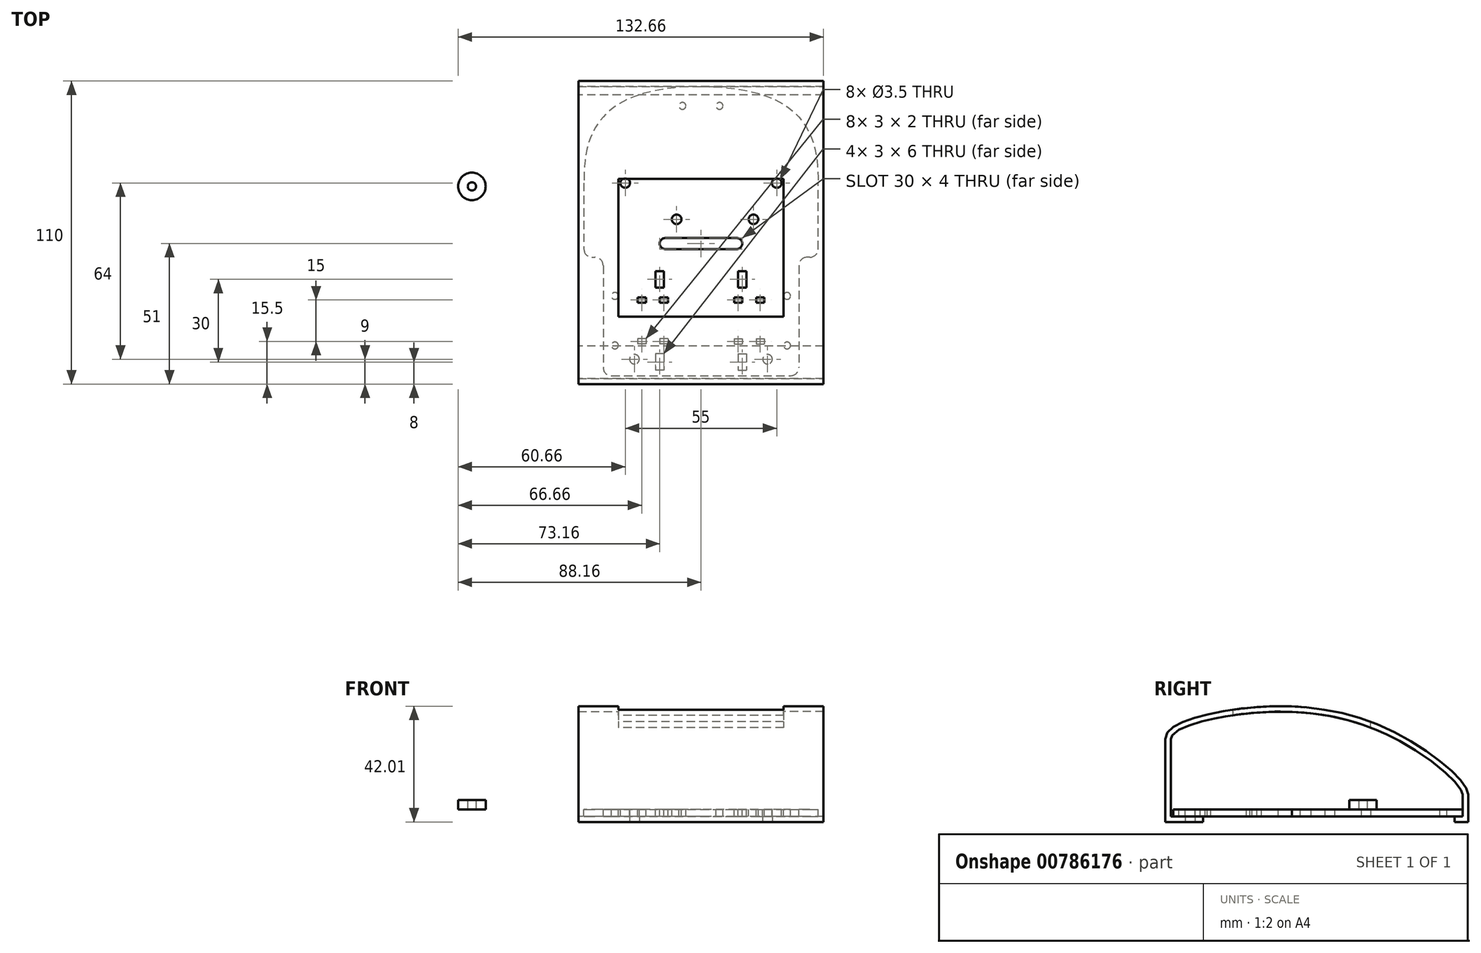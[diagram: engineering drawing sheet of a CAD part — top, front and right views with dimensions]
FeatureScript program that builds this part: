
annotation { "Feature Type Name" : "Feature", "Feature Type Description" : "" }
export const myFeature = defineFeature(function(context is Context, id is Id, definition is map)
    precondition{}
    {
        {
            var Q0;
            Q0=qCreatedBy(makeId("Top.planeOp"),FACE);
            var sketch = newSketch(context, id + "F0", { "sketchPlane" : qUnion([Q0])});
            skPoint(sketch, "E0.middle", {"position": v(0, 0) * mm});
            skLineSegment(sketch, "E1", {"start": v(4.5, 6) * mm, "end": v(31.5, 6) * mm});
            skLineSegment(sketch, "E2", {"start": v(31.5, 6) * mm, "end": v(31.5, -6) * mm});
            skLineSegment(sketch, "E3", {"start": v(31.5, -6) * mm, "end": v(5.5, -6) * mm});
            skLineSegment(sketch, "E4.bottom", {"start": v(20, 6.5) * mm, "end": v(17, 6.5) * mm});
            skLineSegment(sketch, "E4.top", {"start": v(20, 8.5) * mm, "end": v(17, 8.5) * mm});
            skLineSegment(sketch, "E4.left", {"start": v(20, 6.5) * mm, "end": v(20, 8.5) * mm});
            skLineSegment(sketch, "E4.right", {"start": v(17, 6.5) * mm, "end": v(17, 8.5) * mm});
            skPoint(sketch, "E4.middle", {"position": v(18.5, 7.5) * mm});
            skLineSegment(sketch, "E5.bottom", {"start": v(25, 8.5) * mm, "end": v(28, 8.5) * mm});
            skLineSegment(sketch, "E5.top", {"start": v(25, 6.5) * mm, "end": v(28, 6.5) * mm});
            skLineSegment(sketch, "E5.left", {"start": v(25, 8.5) * mm, "end": v(25, 6.5) * mm});
            skLineSegment(sketch, "E5.right", {"start": v(28, 8.5) * mm, "end": v(28, 6.5) * mm});
            skPoint(sketch, "E5.middle", {"position": v(26.5, 7.5) * mm});
            skLineSegment(sketch, "E6", {"start": v(40, -20) * mm, "end": v(40, -20) * mm});
            skLineSegment(sketch, "E7.bottom", {"start": v(26.5, -12) * mm, "end": v(23.5, -12) * mm});
            skLineSegment(sketch, "E7.top", {"start": v(26.5, -18) * mm, "end": v(23.5, -18) * mm});
            skLineSegment(sketch, "E7.left", {"start": v(26.5, -12) * mm, "end": v(26.5, -18) * mm});
            skLineSegment(sketch, "E7.right", {"start": v(23.5, -12) * mm, "end": v(23.5, -18) * mm});
            skPoint(sketch, "E7.middle", {"position": v(25, -15) * mm});
            skLineSegment(sketch, "E8.bottom", {"start": v(23.5, 12) * mm, "end": v(26.5, 12) * mm});
            skLineSegment(sketch, "E8.top", {"start": v(23.5, 18) * mm, "end": v(26.5, 18) * mm});
            skLineSegment(sketch, "E8.left", {"start": v(23.5, 12) * mm, "end": v(23.5, 18) * mm});
            skLineSegment(sketch, "E8.right", {"start": v(26.5, 12) * mm, "end": v(26.5, 18) * mm});
            skPoint(sketch, "E8.middle", {"position": v(25, 15) * mm});
            skCircle(sketch, "E9", {"center": v(8.75, 9) * mm, "radius": 1.25 * mm});
            skCircle(sketch, "E10", {"center": v(8.75, -9) * mm, "radius": 1.25 * mm});
            skCircle(sketch, "E11", {"center": v(12.5, 50) * mm, "radius": 1.75 * mm});
            skLineSegment(sketch, "E12", {"start": v(0.5, 23) * mm, "end": v(1.5, 23) * mm});
            skLineSegment(sketch, "E13", {"start": v(4.5, 20) * mm, "end": v(4.5, -17) * mm});
            skLineSegment(sketch, "E14", {"start": v(7.5, -20) * mm, "end": v(40, -20) * mm});
            skLineSegment(sketch, "E15", {"start": v(40, 85) * mm, "end": v(-2.5, 85) * mm});
            skLineSegment(sketch, "E16", {"start": v(-2.5, 85) * mm, "end": v(-2.5, 26) * mm});
            skLineSegment(sketch, "E17", {"start": v(40, -20) * mm, "end": v(40, 85) * mm, "construction": true});
            skLineSegment(sketch, "E18", {"start": v(7.5, 60) * mm, "end": v(7.5, 65) * mm});
            skLineSegment(sketch, "E19", {"start": v(12.5, 70) * mm, "end": v(40, 70) * mm});
            skLineSegment(sketch, "E20", {"start": v(19.5, 48) * mm, "end": v(40, 48) * mm});
            skLineSegment(sketch, "E21", {"start": v(17.5, 50) * mm, "end": v(17.5, 50) * mm});
            skLineSegment(sketch, "E22", {"start": v(12.5, 55) * mm, "end": v(12.5, 55) * mm});
            skCircle(sketch, "E23", {"center": v(33.27, 78) * mm, "radius": 1.25 * mm});
            skPoint(sketch, "E24.visualSharp", {"position": v(7.5, 70) * mm});
            skArc(sketch, "E24.filletArc", {"start": v(12.5, 70) * mm, "mid": v(8.96, 68.54) * mm, "end": v(7.5, 65) * mm});
            skPoint(sketch, "E25.visualSharp", {"position": v(7.5, 55) * mm});
            skArc(sketch, "E25.filletArc", {"start": v(7.5, 60) * mm, "mid": v(8.96, 56.46) * mm, "end": v(12.5, 55) * mm});
            skPoint(sketch, "E26.visualSharp", {"position": v(17.5, 55) * mm});
            skArc(sketch, "E26.filletArc", {"start": v(17.5, 50) * mm, "mid": v(16.04, 53.54) * mm, "end": v(12.5, 55) * mm});
            skPoint(sketch, "E27.visualSharp", {"position": v(17.5, 48) * mm});
            skArc(sketch, "E27.filletArc", {"start": v(17.5, 50) * mm, "mid": v(18.09, 48.59) * mm, "end": v(19.5, 48) * mm});
            skPoint(sketch, "E28.visualSharp", {"position": v(-2.5, 23) * mm});
            skArc(sketch, "E28.filletArc", {"start": v(-2.5, 26) * mm, "mid": v(-1.62, 23.88) * mm, "end": v(0.5, 23) * mm});
            skPoint(sketch, "E29.visualSharp", {"position": v(4.5, 23) * mm});
            skArc(sketch, "E29.filletArc", {"start": v(4.5, 20) * mm, "mid": v(3.62, 22.12) * mm, "end": v(1.5, 23) * mm});
            skPoint(sketch, "E30.visualSharp", {"position": v(4.5, -20) * mm});
            skArc(sketch, "E30.filletArc", {"start": v(4.5, -17) * mm, "mid": v(5.38, -19.12) * mm, "end": v(7.5, -20) * mm});
            skCircle(sketch, "E31", {"center": v(15.85, -14) * mm, "radius": 1.75 * mm});
            skCircle(sketch, "E32", {"center": v(64.15, -14) * mm, "radius": 1.75 * mm});
            skCircle(sketch, "E33", {"center": v(59.05, 36.8) * mm, "radius": 1.75 * mm});
            skCircle(sketch, "E34", {"center": v(31.15, 36.8) * mm, "radius": 1.75 * mm});
            skLineSegment(sketch, "E35.bottom", {"start": v(-2.5, -20) * mm, "end": v(2.5, -20) * mm});
            skLineSegment(sketch, "E35.top", {"start": v(-2.5, 20) * mm, "end": v(2.5, 20) * mm});
            skLineSegment(sketch, "E35.left", {"start": v(-2.5, -20) * mm, "end": v(-2.5, 20) * mm});
            skLineSegment(sketch, "E35.right", {"start": v(2.5, -20) * mm, "end": v(2.5, 20) * mm});
            skLineSegment(sketch, "E36", {"start": v(0, 0) * mm, "end": v(100, 0) * mm, "construction": true});
            skLineSegment(sketch, "E37.bottom", {"start": v(28, -6.5) * mm, "end": v(25, -6.5) * mm});
            skLineSegment(sketch, "E37.top", {"start": v(28, -8.5) * mm, "end": v(25, -8.5) * mm});
            skLineSegment(sketch, "E37.left", {"start": v(28, -6.5) * mm, "end": v(28, -8.5) * mm});
            skLineSegment(sketch, "E37.right", {"start": v(25, -6.5) * mm, "end": v(25, -8.5) * mm});
            skPoint(sketch, "E37.middle", {"position": v(26.5, -7.5) * mm});
            skLineSegment(sketch, "E38.bottom", {"start": v(20, -6.5) * mm, "end": v(17, -6.5) * mm});
            skLineSegment(sketch, "E38.top", {"start": v(20, -8.5) * mm, "end": v(17, -8.5) * mm});
            skLineSegment(sketch, "E38.left", {"start": v(20, -6.5) * mm, "end": v(20, -8.5) * mm});
            skLineSegment(sketch, "E38.right", {"start": v(17, -6.5) * mm, "end": v(17, -8.5) * mm});
            skPoint(sketch, "E38.middle", {"position": v(18.5, -7.5) * mm});
            skPoint(sketch, "E38.middle.positionSnap0", {"position": v(18.5, 6.5) * mm});
            skPoint(sketch, "E38.centerSnap0", {"position": v(18.5, 6.5) * mm});
            skFitSpline(sketch, "E39", {"points": [v(40, 85) * mm, v(-2.5, 50) * mm], "startDerivative": vector(-120, 0) * mm, "endDerivative": vector(0, -45) * mm});
            skLineSegment(sketch, "E40", {"start": v(40, 30) * mm, "end": v(27, 30) * mm});
            skLineSegment(sketch, "E41", {"start": v(25, 28) * mm, "end": v(25, 28) * mm});
            skLineSegment(sketch, "E42", {"start": v(27, 26) * mm, "end": v(40, 26) * mm});
            skPoint(sketch, "E43.visualSharp", {"position": v(25, 26) * mm});
            skArc(sketch, "E43.filletArc", {"start": v(25, 28) * mm, "mid": v(25.59, 26.59) * mm, "end": v(27, 26) * mm});
            skPoint(sketch, "E44.visualSharp", {"position": v(25, 30) * mm});
            skArc(sketch, "E44.filletArc", {"start": v(27, 30) * mm, "mid": v(25.59, 29.41) * mm, "end": v(25, 28) * mm});
            skArc(sketch, "E45.MirrorCS", {"start": v(82.5, 26) * mm, "mid": v(81.62, 23.88) * mm, "end": v(79.5, 23) * mm});
            skArc(sketch, "E46.MirrorCS", {"start": v(75.5, 20) * mm, "mid": v(76.38, 22.12) * mm, "end": v(78.5, 23) * mm});
            skLineSegment(sketch, "E47.MirrorCS", {"start": v(82.5, 20) * mm, "end": v(77.5, 20) * mm});
            skArc(sketch, "E48.MirrorCS", {"start": v(53, 30) * mm, "mid": v(54.41, 29.41) * mm, "end": v(55, 28) * mm});
            skLineSegment(sketch, "E49.MirrorCS", {"start": v(60, 6.5) * mm, "end": v(63, 6.5) * mm});
            skLineSegment(sketch, "E50.MirrorCS", {"start": v(55, -6.5) * mm, "end": v(55, -8.5) * mm});
            skLineSegment(sketch, "E51.MirrorCS", {"start": v(60, 8.5) * mm, "end": v(63, 8.5) * mm});
            skLineSegment(sketch, "E52.MirrorCS", {"start": v(60, 6.5) * mm, "end": v(60, 8.5) * mm});
            skArc(sketch, "E53.MirrorCS", {"start": v(55, 28) * mm, "mid": v(54.41, 26.59) * mm, "end": v(53, 26) * mm});
            skLineSegment(sketch, "E54.MirrorCS", {"start": v(55, 8.5) * mm, "end": v(55, 6.5) * mm});
            skLineSegment(sketch, "E55.MirrorCS", {"start": v(60, -6.5) * mm, "end": v(60, -8.5) * mm});
            skLineSegment(sketch, "E56.MirrorCS", {"start": v(63, 6.5) * mm, "end": v(63, 8.5) * mm});
            skLineSegment(sketch, "E57.MirrorCS", {"start": v(52, 8.5) * mm, "end": v(52, 6.5) * mm});
            skLineSegment(sketch, "E58.MirrorCS", {"start": v(52, -8.5) * mm, "end": v(55, -8.5) * mm});
            skLineSegment(sketch, "E59.MirrorCS", {"start": v(56.5, 18) * mm, "end": v(53.5, 18) * mm});
            skLineSegment(sketch, "E60.MirrorCS", {"start": v(53.5, -12) * mm, "end": v(56.5, -12) * mm});
            skLineSegment(sketch, "E61.MirrorCS", {"start": v(60, -8.5) * mm, "end": v(63, -8.5) * mm});
            skLineSegment(sketch, "E62.MirrorCS", {"start": v(63, -6.5) * mm, "end": v(63, -8.5) * mm});
            skLineSegment(sketch, "E63.MirrorCS", {"start": v(56.5, 12) * mm, "end": v(53.5, 12) * mm});
            skLineSegment(sketch, "E64.MirrorCS", {"start": v(60, -6.5) * mm, "end": v(63, -6.5) * mm});
            skLineSegment(sketch, "E65.MirrorCS", {"start": v(53.5, 12) * mm, "end": v(53.5, 18) * mm});
            skArc(sketch, "E66.MirrorCS", {"start": v(75.5, -17) * mm, "mid": v(74.62, -19.12) * mm, "end": v(72.5, -20) * mm});
            skLineSegment(sketch, "E67.MirrorCS", {"start": v(55, 8.5) * mm, "end": v(52, 8.5) * mm});
            skLineSegment(sketch, "E68.MirrorCS", {"start": v(55, 6.5) * mm, "end": v(52, 6.5) * mm});
            skLineSegment(sketch, "E69.MirrorCS", {"start": v(52, -6.5) * mm, "end": v(55, -6.5) * mm});
            skLineSegment(sketch, "E70.MirrorCS", {"start": v(56.5, 12) * mm, "end": v(56.5, 18) * mm});
            skArc(sketch, "E71.MirrorCS", {"start": v(62.5, 50) * mm, "mid": v(63.96, 53.54) * mm, "end": v(67.5, 55) * mm});
            skLineSegment(sketch, "E72.MirrorCS", {"start": v(52, -6.5) * mm, "end": v(52, -8.5) * mm});
            skLineSegment(sketch, "E73.MirrorCS", {"start": v(67.5, 55) * mm, "end": v(67.5, 55) * mm});
            skCircle(sketch, "E74.MirrorC", {"center": v(67.5, 50) * mm, "radius": 1.75 * mm});
            skLineSegment(sketch, "E75.MirrorCS", {"start": v(53.5, -18) * mm, "end": v(56.5, -18) * mm});
            skLineSegment(sketch, "E76.MirrorCS", {"start": v(56.5, -12) * mm, "end": v(56.5, -18) * mm});
            skLineSegment(sketch, "E77.MirrorCS", {"start": v(75.5, 6) * mm, "end": v(48.5, 6) * mm});
            skCircle(sketch, "E78.MirrorC", {"center": v(71.25, 9) * mm, "radius": 1.25 * mm});
            skArc(sketch, "E79.MirrorCS", {"start": v(67.5, 70) * mm, "mid": v(71.04, 68.54) * mm, "end": v(72.5, 65) * mm});
            skLineSegment(sketch, "E80.MirrorCS", {"start": v(53.5, -12) * mm, "end": v(53.5, -18) * mm});
            skLineSegment(sketch, "E81.MirrorCS", {"start": v(82.5, -20) * mm, "end": v(77.5, -20) * mm});
            skCircle(sketch, "E82.MirrorC", {"center": v(71.25, -9) * mm, "radius": 1.25 * mm});
            skArc(sketch, "E83.MirrorCS", {"start": v(72.5, 60) * mm, "mid": v(71.04, 56.46) * mm, "end": v(67.5, 55) * mm});
            skArc(sketch, "E84.MirrorCS", {"start": v(62.5, 50) * mm, "mid": v(61.91, 48.59) * mm, "end": v(60.5, 48) * mm});
            skLineSegment(sketch, "E85.MirrorCS", {"start": v(75.5, 20) * mm, "end": v(75.5, -17) * mm});
            skLineSegment(sketch, "E86.MirrorCS", {"start": v(48.5, 6) * mm, "end": v(48.5, -6) * mm});
            skPoint(sketch, "E87.MirrorP", {"position": v(61.5, 6.5) * mm});
            skPoint(sketch, "E88.MirrorP", {"position": v(80, 0) * mm});
            skLineSegment(sketch, "E89.MirrorCS", {"start": v(53, 26) * mm, "end": v(40, 26) * mm});
            skLineSegment(sketch, "E90.MirrorCS", {"start": v(77.5, -20) * mm, "end": v(77.5, 20) * mm});
            skLineSegment(sketch, "E91.MirrorCS", {"start": v(48.5, -6) * mm, "end": v(74.5, -6) * mm});
            skCircle(sketch, "E92.MirrorC", {"center": v(46.73, 78) * mm, "radius": 1.25 * mm});
            skLineSegment(sketch, "E93.MirrorCS", {"start": v(72.5, 60) * mm, "end": v(72.5, 65) * mm});
            skPoint(sketch, "E94.MirrorP", {"position": v(53.5, -7.5) * mm});
            skPoint(sketch, "E95.MirrorP", {"position": v(55, 26) * mm});
            skFitSpline(sketch, "E96.MirrorCS", {"points": [v(40, 85) * mm, v(82.5, 50) * mm], "startDerivative": vector(120, 0) * mm, "endDerivative": vector(0, -45) * mm});
            skPoint(sketch, "E97.MirrorP", {"position": v(55, 30) * mm});
            skLineSegment(sketch, "E98.MirrorCS", {"start": v(40, 30) * mm, "end": v(53, 30) * mm});
            skPoint(sketch, "E99.MirrorP", {"position": v(72.5, 70) * mm});
            skLineSegment(sketch, "E100.MirrorCS", {"start": v(72.5, -20) * mm, "end": v(40, -20) * mm});
            skLineSegment(sketch, "E101.MirrorCS", {"start": v(60.5, 48) * mm, "end": v(40, 48) * mm});
            skPoint(sketch, "E102.MirrorP", {"position": v(82.5, 23) * mm});
            skPoint(sketch, "E103.MirrorP", {"position": v(61.5, 7.5) * mm});
            skLineSegment(sketch, "E104.MirrorCS", {"start": v(82.5, -20) * mm, "end": v(82.5, 20) * mm});
            skPoint(sketch, "E105.MirrorP", {"position": v(62.5, 48) * mm});
            skPoint(sketch, "E106.MirrorP", {"position": v(75.5, -20) * mm});
            skPoint(sketch, "E107.MirrorP", {"position": v(53.5, 7.5) * mm});
            skLineSegment(sketch, "E108.MirrorCS", {"start": v(67.5, 70) * mm, "end": v(40, 70) * mm});
            skPoint(sketch, "E109.MirrorP", {"position": v(72.5, 55) * mm});
            skPoint(sketch, "E110.MirrorP", {"position": v(62.5, 55) * mm});
            skPoint(sketch, "E111.MirrorP", {"position": v(55, 15) * mm});
            skPoint(sketch, "E112.MirrorP", {"position": v(75.5, 23) * mm});
            skPoint(sketch, "E113.MirrorP", {"position": v(61.5, -7.5) * mm});
            skPoint(sketch, "E114.MirrorP", {"position": v(55, -15) * mm});
            skLineSegment(sketch, "E115.MirrorCS", {"start": v(40, 85) * mm, "end": v(82.5, 85) * mm});
            skLineSegment(sketch, "E116", {"start": v(82.5, 26) * mm, "end": v(82.5, 50) * mm});
            skPoint(sketch, "E117", {"position": v(18.5, -6) * mm});
            skLineSegment(sketch, "E118", {"start": v(5.5, -6) * mm, "end": v(4.5, -6) * mm});
            skLineSegment(sketch, "E119", {"start": v(74.5, -6) * mm, "end": v(75.5, -6) * mm});
            skLineSegment(sketch, "E120", {"start": v(79.5, 23) * mm, "end": v(78.5, 23) * mm});
            skSolve(sketch);
        }
        {
            var Q0;
            {var subQ1=sQuery(id+"F0.wireOp",EDGE,"E1");Q0=makeQuery(id+"F0.imprint","IMPRINT",FACE,{"disambiguationData":[TD([[makeQuery(id+"F0.imprint","IMPRINT",EDGE,{"derivedFrom":subQ1}),-1.0]])]});}
            var Q1;
            {var subQ0=sQuery(id+"F0.wireOp",EDGE,"E77.MirrorCS");Q1=makeQuery(id+"F0.imprint","IMPRINT",FACE,{"disambiguationData":[TD([[makeQuery(id+"F0.imprint","IMPRINT",EDGE,{"derivedFrom":subQ0}),1.0]])]});}
            var Q2;
            Q2=makeQuery(id+"F0.imprint","IMPRINT",FACE,{"disambiguationData":[TD([[makeQuery(id+"F0.imprint","IMPRINT",EDGE,{"derivedFrom":sQuery(id+"F0.wireOp",EDGE,"E18")}),-1.0]])]});
            var Q3;
            {var subQ4=sQuery(id+"F0.wireOp",EDGE,"E1");Q3=makeQuery(id+"F0.imprint","IMPRINT",FACE,{"disambiguationData":[TD([[makeQuery(id+"F0.imprint","IMPRINT",EDGE,{"derivedFrom":subQ4}),1.0]])]});}
            extrude(context, id + "F1", {"entities" : qUnion([Q0, Q1, Q2, Q3]), "oppositeDirection" : true, "depth" : 2.5 * mm, "offsetDistance" : 25 * mm});
        }
        {
            var Q0;
            Q0=qCreatedBy(makeId("Top.planeOp"),FACE);
            var sketch = newSketch(context, id + "F2", { "sketchPlane" : qUnion([Q0])});
            skCircle(sketch, "E121", {"center": v(-43.16, 48.77) * mm, "radius": 1.5 * mm});
            skCircle(sketch, "E122", {"center": v(-43.16, 48.77) * mm, "radius": 5 * mm});
            skSolve(sketch);
        }
        {
            var Q0;
            Q0=makeQuery(id+"F2.imprint","IMPRINT",FACE,{"disambiguationData":[TD([[makeQuery(id+"F2.imprint","IMPRINT",EDGE,{"derivedFrom":sQuery(id+"F2.wireOp",EDGE,"E121")}),-1.0]])]});
            extrude(context, id + "F3", {"entities" : qUnion([Q0]), "depth" : 3.5 * mm, "offsetDistance" : 25 * mm});
        }
        {
            var Q0;
            Q0=qCreatedBy(makeId("Right.planeOp"),FACE);
            cPlane(context, id + "F4", {"entities" : qUnion([Q0]), "cplaneType" : CPlaneType.OFFSET, "offset" : 40 * mm, "width" : 150 * mm, "height" : 150 * mm});
        }
        {
            var Q0;
            Q0=qCreatedBy(id+"F4.planeOp",FACE);
            var sketch = newSketch(context, id + "F5", { "sketchPlane" : qUnion([Q0])});
            skLineSegment(sketch, "E123.0", {"start": v(-15.75, -2.5) * mm, "end": v(-12.25, -2.5) * mm});
            skPoint(sketch, "E124.0", {"position": v(-20, -2.5) * mm});
            skLineSegment(sketch, "E125.0", {"start": v(85, -2.5) * mm, "end": v(85, 0) * mm});
            skLineSegment(sketch, "E126", {"start": v(-12.25, -2.5) * mm, "end": v(-9.25, -2.5) * mm});
            skLineSegment(sketch, "E127", {"start": v(-9.25, -2.5) * mm, "end": v(-9.25, -4.5) * mm});
            skLineSegment(sketch, "E128", {"start": v(-9.25, -4.5) * mm, "end": v(-23, -4.5) * mm});
            skLineSegment(sketch, "E129", {"start": v(-23, -4.5) * mm, "end": v(-23, 25.5) * mm});
            skLineSegment(sketch, "E130", {"start": v(-15.75, -2.5) * mm, "end": v(-21, -2.5) * mm});
            skLineSegment(sketch, "E131", {"start": v(85, -2.5) * mm, "end": v(82, -2.5) * mm});
            skLineSegment(sketch, "E132", {"start": v(82, -2.5) * mm, "end": v(82, -4.5) * mm});
            skLineSegment(sketch, "E133", {"start": v(82, -4.5) * mm, "end": v(87, -4.5) * mm});
            skLineSegment(sketch, "E134", {"start": v(87, -4.5) * mm, "end": v(87, 5.5) * mm});
            skFitSpline(sketch, "E135", {"points": [v(-23, 25.5) * mm, v(-3, 35.5) * mm, v(55, 30.5) * mm, v(87, 5.5) * mm], "startDerivative": vector(0, 59.42) * mm, "endDerivative": vector(0, -44.1) * mm});
            skLineSegment(sketch, "E136.0", {"start": v(85, 0) * mm, "end": v(85, 5.5) * mm});
            skFitSpline(sketch, "E136.1", {"points": [v(-21, 25.5) * mm, v(-21, 25.58) * mm, v(-21, 25.73) * mm, v(-20.95, 25.95) * mm, v(-20.89, 26.17) * mm, v(-20.8, 26.4) * mm, v(-20.66, 26.64) * mm, v(-20.43, 26.99) * mm, v(-20.03, 27.44) * mm, v(-19.37, 28.03) * mm, v(-18.52, 28.62) * mm, v(-17.5, 29.2) * mm, v(-16.33, 29.78) * mm, v(-15, 30.33) * mm, v(-13.08, 31.04) * mm, v(-10.92, 31.69) * mm, v(-8.6, 32.29) * mm, v(-6.77, 32.71) * mm, v(-4.9, 33.1) * mm, v(-3.28, 33.42) * mm, v(-1.97, 33.65) * mm, v(-0.65, 33.88) * mm, v(1.02, 34.15) * mm, v(3.05, 34.44) * mm, v(5.79, 34.79) * mm, v(9.28, 35.14) * mm, v(13.56, 35.42) * mm, v(17.9, 35.53) * mm, v(22.32, 35.48) * mm, v(26.77, 35.23) * mm, v(31.26, 34.78) * mm, v(35.77, 34.1) * mm, v(40.28, 33.2) * mm, v(44.04, 32.23) * mm, v(47.03, 31.33) * mm, v(49.27, 30.58) * mm, v(51.5, 29.77) * mm, v(53.35, 29.03) * mm, v(54.82, 28.4) * mm, v(56.3, 27.75) * mm, v(58.12, 26.9) * mm, v(60.3, 25.8) * mm, v(63.15, 24.27) * mm, v(66.62, 22.24) * mm, v(70.54, 19.7) * mm, v(74.14, 17.11) * mm, v(77.37, 14.55) * mm, v(79.68, 12.5) * mm, v(81.26, 10.93) * mm, v(82.3, 9.82) * mm, v(83.19, 8.78) * mm, v(83.9, 7.82) * mm, v(84.36, 7.1) * mm, v(84.63, 6.6) * mm, v(84.79, 6.27) * mm, v(84.9, 5.98) * mm, v(84.97, 5.75) * mm, v(85, 5.58) * mm, v(85, 5.52) * mm, v(85, 5.5) * mm]});
            skLineSegment(sketch, "E136.2", {"start": v(-21, -2.5) * mm, "end": v(-21, 25.5) * mm});
            skSolve(sketch);
        }
        {
            var Q0;
            Q0=makeQuery(id+"F5.imprint","IMPRINT",FACE,{"disambiguationData":[TD([[makeQuery(id+"F5.imprint","IMPRINT",EDGE,{"derivedFrom":sQuery(id+"F5.wireOp",EDGE,"E123.0")}),-1.0]])]});
            var Q1;
            Q1=makeQuery(id+"F1.opExtrude","SWEPT_FACE",FACE,{"disambiguationData":[OSD([sQuery(id+"F0.wireOp",EDGE,"E116")])]});
            var Q2;
            Q2=makeQuery(id+"F1.opExtrude","SWEPT_FACE",FACE,{"disambiguationData":[OSD([sQuery(id+"F0.wireOp",EDGE,"E16")])]});
            extrude(context, id + "F6", {"entities" : qUnion([Q0]), "endBound" : BoundingType.UP_TO_SURFACE, "depth" : 25 * mm, "endBoundEntityFace" : qUnion([Q1]), "hasOffset" : true, "offsetDistance" : 2 * mm, "offsetOppositeDirection" : true, "hasSecondDirection" : true, "secondDirectionBound" : SecondDirectionBoundingType.UP_TO_SURFACE, "secondDirectionOppositeDirection" : true, "secondDirectionDepth" : 25 * mm, "secondDirectionBoundEntityFace" : qUnion([Q2]), "hasSecondDirectionOffset" : true, "secondDirectionOffsetDistance" : 2 * mm, "secondDirectionOffsetOppositeDirection" : true});
        }
        {
            var Q0;
            {var subQ0=sQuery(id+"F5.wireOp",EDGE,"E133");var subQ1=sQuery(id+"F5.wireOp",EDGE,"E128");Q0=makeQuery(id+"FgIjVRS8KDGZvRM_3.boolean.opBoolean","MERGE",FACE,{"derivedFrom":[makeQuery(id+"F4yyrsu4QSFDEXo_3.boolean.opBoolean","MERGE",FACE,{"derivedFrom":[makeQuery(id+"F6.opExtrude","SWEPT_FACE",FACE,{"disambiguationData":[OSD([subQ1])]}),makeQuery(id+"F6.opExtrude","SWEPT_FACE",FACE,{"disambiguationData":[OSD([subQ0])]}),makeQuery(id+"F4yyrsu4QSFDEXo_3.opExtrude","SWEPT_FACE",FACE,{"disambiguationData":[OSD([sQuery(id+"FKcrgtSKjOyZDcc_3.wireOp",EDGE,"879abbe2-a129-44d6-996e-69aa2a97fe4d.0"),sQuery(id+"FKcrgtSKjOyZDcc_3.wireOp",EDGE,"762b29cf-0b08-470c-bd98-8940d6be20b4.0"),sQuery(id+"FKcrgtSKjOyZDcc_3.wireOp",EDGE,"eguiDy1r-vEaW-etDs-xl0Y-iHVzydblselK")])]})]}),makeQuery(id+"FgIjVRS8KDGZvRM_3.opExtrude","SWEPT_FACE",FACE,{"disambiguationData":[OSD([subQ1,subQ0,sQuery(id+"FLf3MJlWTwCFmlf_3.wireOp",EDGE,"mTxCMDkh-dDiF-zmkk-8dRB-iNjdKrWSOVnO")])]})]});}
            var sketch = newSketch(context, id + "F7", { "sketchPlane" : qUnion([Q0])});
            skCircle(sketch, "E137.0", {"center": v(64.15, 14) * mm, "radius": 1.75 * mm});
            skCircle(sketch, "E138.0", {"center": v(15.85, 14) * mm, "radius": 1.75 * mm});
            skSolve(sketch);
        }
        {
            var Q0;
            Q0=makeQuery(id+"F7.imprint","IMPRINT",FACE,{"disambiguationData":[TD([[makeQuery(id+"F7.imprint","IMPRINT",EDGE,{"derivedFrom":sQuery(id+"F7.wireOp",EDGE,"E137.0")}),1.0]])]});
            var Q1;
            Q1=makeQuery(id+"F7.imprint","IMPRINT",FACE,{"disambiguationData":[TD([[makeQuery(id+"F7.imprint","IMPRINT",EDGE,{"derivedFrom":sQuery(id+"F7.wireOp",EDGE,"E138.0")}),1.0]])]});
            var Q2;
            Q2=makeQuery(id+"F1.opExtrude","CAP_FACE",FACE,{"disambiguationData":[OSD([sQuery(id+"F0.wireOp",EDGE,"E4.bottom"),sQuery(id+"F0.wireOp",EDGE,"E4.top"),sQuery(id+"F0.wireOp",EDGE,"E4.left"),sQuery(id+"F0.wireOp",EDGE,"E4.right"),sQuery(id+"F0.wireOp",EDGE,"E5.bottom"),sQuery(id+"F0.wireOp",EDGE,"E5.top"),sQuery(id+"F0.wireOp",EDGE,"E5.left"),sQuery(id+"F0.wireOp",EDGE,"E5.right"),sQuery(id+"F0.wireOp",EDGE,"E7.bottom"),sQuery(id+"F0.wireOp",EDGE,"E7.top"),sQuery(id+"F0.wireOp",EDGE,"E7.left"),sQuery(id+"F0.wireOp",EDGE,"E7.right"),sQuery(id+"F0.wireOp",EDGE,"E8.bottom"),sQuery(id+"F0.wireOp",EDGE,"E8.top"),sQuery(id+"F0.wireOp",EDGE,"E8.left"),sQuery(id+"F0.wireOp",EDGE,"E8.right"),sQuery(id+"F0.wireOp",EDGE,"E9"),sQuery(id+"F0.wireOp",EDGE,"E10"),sQuery(id+"F0.wireOp",EDGE,"E11"),sQuery(id+"F0.wireOp",EDGE,"E12"),sQuery(id+"F0.wireOp",EDGE,"E13"),sQuery(id+"F0.wireOp",EDGE,"E14"),sQuery(id+"F0.wireOp",EDGE,"E16"),sQuery(id+"F0.wireOp",EDGE,"E23"),sQuery(id+"F0.wireOp",EDGE,"E28.filletArc"),sQuery(id+"F0.wireOp",EDGE,"E29.filletArc"),sQuery(id+"F0.wireOp",EDGE,"E30.filletArc"),sQuery(id+"F0.wireOp",EDGE,"E31"),sQuery(id+"F0.wireOp",EDGE,"E32"),sQuery(id+"F0.wireOp",EDGE,"E33"),sQuery(id+"F0.wireOp",EDGE,"E34"),sQuery(id+"F0.wireOp",EDGE,"E37.bottom"),sQuery(id+"F0.wireOp",EDGE,"E37.top"),sQuery(id+"F0.wireOp",EDGE,"E37.left"),sQuery(id+"F0.wireOp",EDGE,"E37.right"),sQuery(id+"F0.wireOp",EDGE,"E38.bottom"),sQuery(id+"F0.wireOp",EDGE,"E38.top"),sQuery(id+"F0.wireOp",EDGE,"E38.left"),sQuery(id+"F0.wireOp",EDGE,"E38.right"),sQuery(id+"F0.wireOp",EDGE,"E39"),sQuery(id+"F0.wireOp",EDGE,"E40"),sQuery(id+"F0.wireOp",EDGE,"E42"),sQuery(id+"F0.wireOp",EDGE,"E43.filletArc"),sQuery(id+"F0.wireOp",EDGE,"E44.filletArc"),sQuery(id+"F0.wireOp",EDGE,"E45.MirrorCS"),sQuery(id+"F0.wireOp",EDGE,"E46.MirrorCS"),sQuery(id+"F0.wireOp",EDGE,"E48.MirrorCS"),sQuery(id+"F0.wireOp",EDGE,"E49.MirrorCS"),sQuery(id+"F0.wireOp",EDGE,"E50.MirrorCS"),sQuery(id+"F0.wireOp",EDGE,"E51.MirrorCS"),sQuery(id+"F0.wireOp",EDGE,"E52.MirrorCS"),sQuery(id+"F0.wireOp",EDGE,"E53.MirrorCS"),sQuery(id+"F0.wireOp",EDGE,"E54.MirrorCS"),sQuery(id+"F0.wireOp",EDGE,"E55.MirrorCS"),sQuery(id+"F0.wireOp",EDGE,"E56.MirrorCS"),sQuery(id+"F0.wireOp",EDGE,"E57.MirrorCS"),sQuery(id+"F0.wireOp",EDGE,"E58.MirrorCS"),sQuery(id+"F0.wireOp",EDGE,"E59.MirrorCS"),sQuery(id+"F0.wireOp",EDGE,"E60.MirrorCS"),sQuery(id+"F0.wireOp",EDGE,"E61.MirrorCS"),sQuery(id+"F0.wireOp",EDGE,"E62.MirrorCS"),sQuery(id+"F0.wireOp",EDGE,"E63.MirrorCS"),sQuery(id+"F0.wireOp",EDGE,"E64.MirrorCS"),sQuery(id+"F0.wireOp",EDGE,"E65.MirrorCS"),sQuery(id+"F0.wireOp",EDGE,"E66.MirrorCS"),sQuery(id+"F0.wireOp",EDGE,"E67.MirrorCS"),sQuery(id+"F0.wireOp",EDGE,"E68.MirrorCS"),sQuery(id+"F0.wireOp",EDGE,"E69.MirrorCS"),sQuery(id+"F0.wireOp",EDGE,"E70.MirrorCS"),sQuery(id+"F0.wireOp",EDGE,"E72.MirrorCS"),sQuery(id+"F0.wireOp",EDGE,"E74.MirrorC"),sQuery(id+"F0.wireOp",EDGE,"E75.MirrorCS"),sQuery(id+"F0.wireOp",EDGE,"E76.MirrorCS"),sQuery(id+"F0.wireOp",EDGE,"E78.MirrorC"),sQuery(id+"F0.wireOp",EDGE,"E80.MirrorCS"),sQuery(id+"F0.wireOp",EDGE,"E82.MirrorC"),sQuery(id+"F0.wireOp",EDGE,"E85.MirrorCS"),sQuery(id+"F0.wireOp",EDGE,"E89.MirrorCS"),sQuery(id+"F0.wireOp",EDGE,"E92.MirrorC"),sQuery(id+"F0.wireOp",EDGE,"E96.MirrorCS"),sQuery(id+"F0.wireOp",EDGE,"E98.MirrorCS"),sQuery(id+"F0.wireOp",EDGE,"E100.MirrorCS"),sQuery(id+"F0.wireOp",EDGE,"E116"),sQuery(id+"F0.wireOp",EDGE,"E120")])],"isStart":false});
            extrude(context, id + "F8", {"entities" : qUnion([Q0, Q1]), "operationType" : NewBodyOperationType.REMOVE, "endBound" : BoundingType.UP_TO_SURFACE, "oppositeDirection" : true, "depth" : 25 * mm, "endBoundEntityFace" : qUnion([Q2]), "offsetDistance" : 25 * mm});
        }
        {
            var Q0;
            Q0=qCreatedBy(makeId("Top.planeOp"),FACE);
            var sketch = newSketch(context, id + "F9", { "sketchPlane" : qUnion([Q0])});
            skPoint(sketch, "E139.0", {"position": v(17, 6.5) * mm});
            skPoint(sketch, "E140.0", {"position": v(63, 6.5) * mm});
            skLineSegment(sketch, "E141", {"start": v(10, 1.5) * mm, "end": v(70, 1.5) * mm});
            skLineSegment(sketch, "E142", {"start": v(70, 1.5) * mm, "end": v(70, 51.5) * mm});
            skLineSegment(sketch, "E143", {"start": v(70, 51.5) * mm, "end": v(10, 51.5) * mm});
            skLineSegment(sketch, "E144", {"start": v(10, 51.5) * mm, "end": v(10, 1.5) * mm});
            skLineSegment(sketch, "E145", {"start": v(17, 6.5) * mm, "end": v(10, 6.5) * mm, "construction": true});
            skLineSegment(sketch, "E146", {"start": v(63, 6.5) * mm, "end": v(70, 6.5) * mm, "construction": true});
            skSolve(sketch);
        }
        {
            var Q0;
            Q0=makeQuery(id+"F9.imprint","IMPRINT",FACE,{"disambiguationData":[TD([[makeQuery(id+"F9.imprint","IMPRINT",EDGE,{"derivedFrom":sQuery(id+"F9.wireOp",EDGE,"E141")}),1.0]])]});
            var Q1;
            Q1=makeQuery(id+"F6.opExtrude","SWEPT_FACE",FACE,{"disambiguationData":[OSD([sQuery(id+"F5.wireOp",EDGE,"E135")])]});
            extrude(context, id + "F10", {"entities" : qUnion([Q0]), "operationType" : NewBodyOperationType.REMOVE, "endBound" : BoundingType.UP_TO_SURFACE, "depth" : 25 * mm, "endBoundEntityFace" : qUnion([Q1]), "offsetDistance" : 25 * mm});
        }
    });
